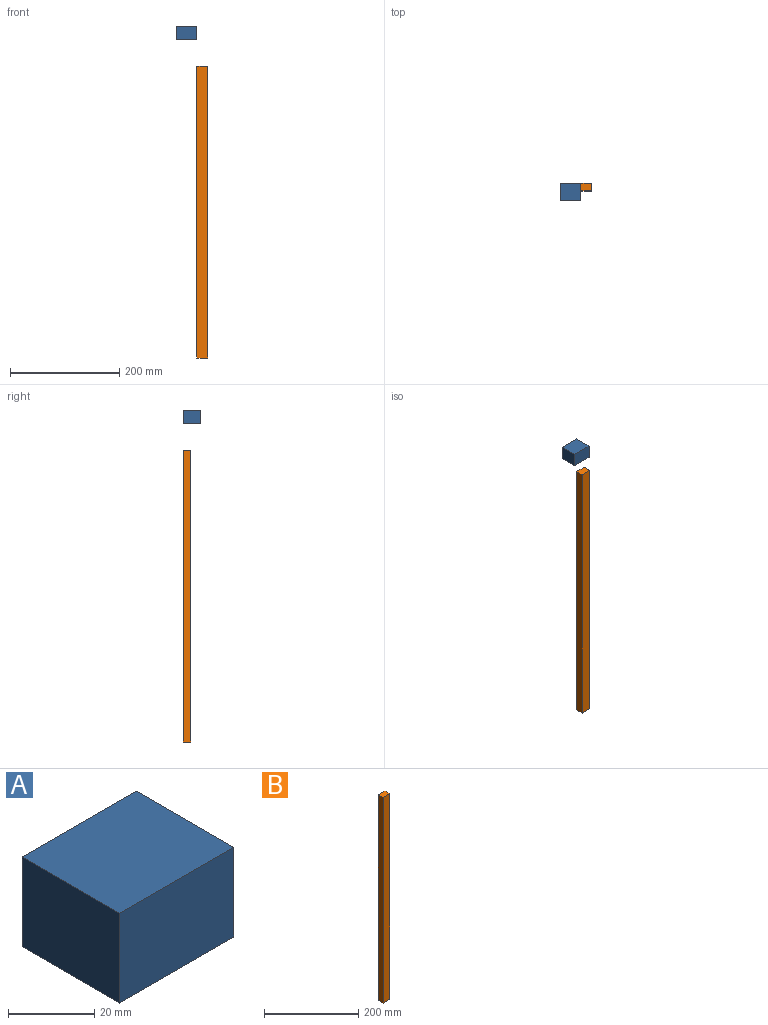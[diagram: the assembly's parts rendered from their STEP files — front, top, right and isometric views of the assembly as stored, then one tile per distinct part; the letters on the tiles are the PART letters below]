
ASSEMBLY  parts=2 mates=1
PART A: 6 faces, bbox 37.4x32x25.4 mm
  f0: plane 37.41x25.4mm, normal (0,1,0), area 950.1mm2, adj f1,f3,f4,f5
  f1: plane 31.96x25.4mm, normal (-1,0,0), area 811.8mm2, adj f0,f2,f4,f5
  f2: plane 37.41x25.4mm, normal (0,-1,0), area 950.1mm2, adj f1,f3,f4,f5
  f3: plane 31.96x25.4mm, normal (1,0,0), area 811.8mm2, adj f0,f2,f4,f5
  f4: plane 37.41x31.96mm, normal (0,0,1), area 1195.6mm2, adj f0,f1,f2,f3
  f5: plane 37.41x31.96mm, normal (0,0,-1), area 1195.6mm2, adj f0,f1,f2,f3
PART B: 6 faces, bbox 19.9x14x533.4 mm
  f0: plane 533.4x19.91mm, normal (0,1,0), area 10617.4mm2, adj f1,f3,f4,f5
  f1: plane 533.4x14.01mm, normal (-1,0,0), area 7470.5mm2, adj f0,f2,f4,f5
  f2: plane 533.4x19.91mm, normal (0,-1,0), area 10617.4mm2, adj f1,f3,f4,f5
  f3: plane 533.4x14.01mm, normal (1,0,0), area 7470.5mm2, adj f0,f2,f4,f5
  f4: plane 19.91x14.01mm, normal (0,0,1), area 278.8mm2, adj f0,f1,f2,f3
  f5: plane 19.91x14.01mm, normal (0,0,-1), area 278.8mm2, adj f0,f1,f2,f3
PLACE A rot(axis=(1,0,0),180deg) t=(48.17,-3.17,21.59)mm
PLACE B t=(84.84,0,-76.96)mm
MATE slider A.f4 <-> B.f4  axis (0,0,-1) through (36.33,-8.85,-3.81)mm
